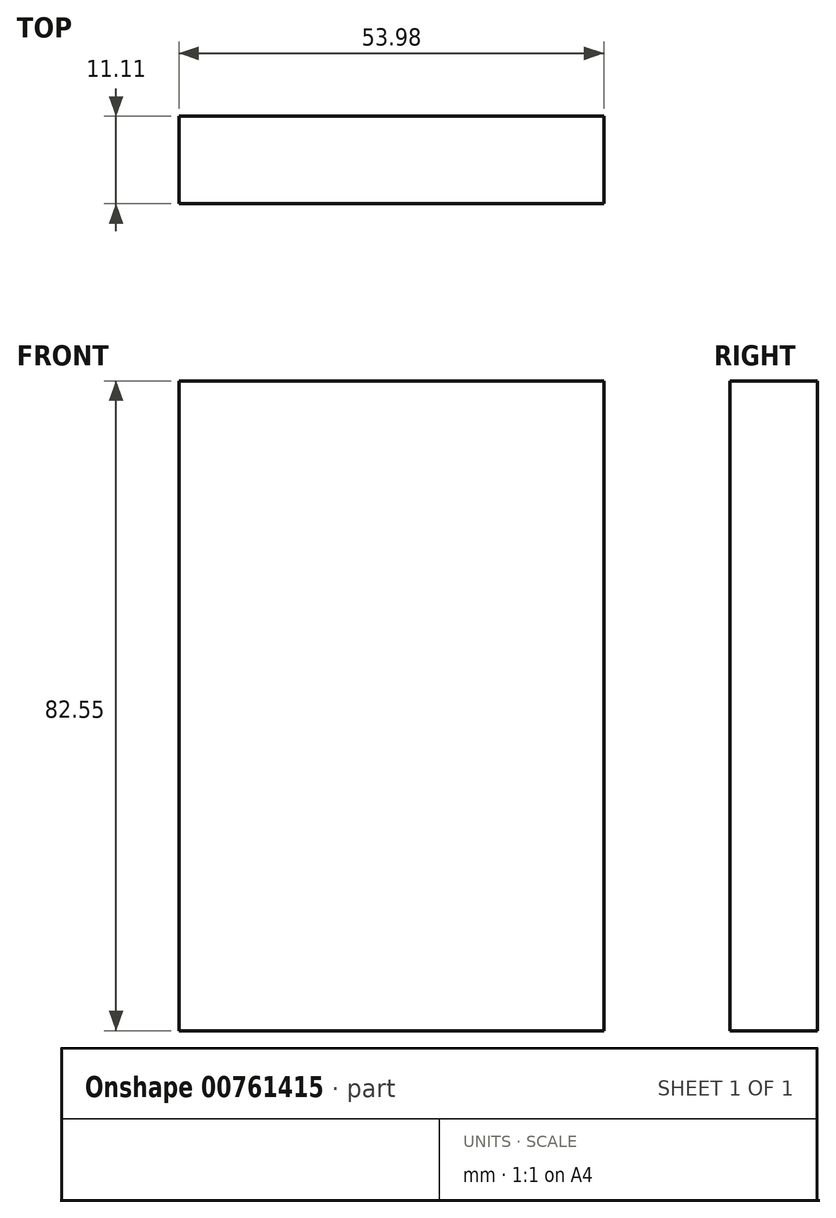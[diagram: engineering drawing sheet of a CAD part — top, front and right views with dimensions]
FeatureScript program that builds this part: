
annotation { "Feature Type Name" : "Feature", "Feature Type Description" : "" }
export const myFeature = defineFeature(function(context is Context, id is Id, definition is map)
    precondition{}
    {
        {
            var Q0;
            Q0=qCreatedBy(makeId("Front.planeOp"),FACE);
            var sketch = newSketch(context, id + "F0", { "sketchPlane" : qUnion([Q0])});
            skLineSegment(sketch, "E0.bottom", {"start": v(0, 0) * mm, "end": v(53.98, 0) * mm});
            skLineSegment(sketch, "E0.top", {"start": v(0, -82.55) * mm, "end": v(53.98, -82.55) * mm});
            skLineSegment(sketch, "E0.left", {"start": v(0, 0) * mm, "end": v(0, -82.55) * mm});
            skLineSegment(sketch, "E0.right", {"start": v(53.98, 0) * mm, "end": v(53.98, -82.55) * mm});
            skSolve(sketch);
        }
        {
            var Q0;
            Q0=makeQuery(id+"F0.imprint","IMPRINT",FACE,{"disambiguationData":[TD([[makeQuery(id+"F0.imprint","IMPRINT",EDGE,{"derivedFrom":sQuery(id+"F0.wireOp",EDGE,"E0.bottom")}),-1.0]])]});
            extrude(context, id + "F1", {"entities" : qUnion([Q0]), "depth" : 11.1 * mm, "offsetDistance" : 25.4 * mm});
        }
    });
